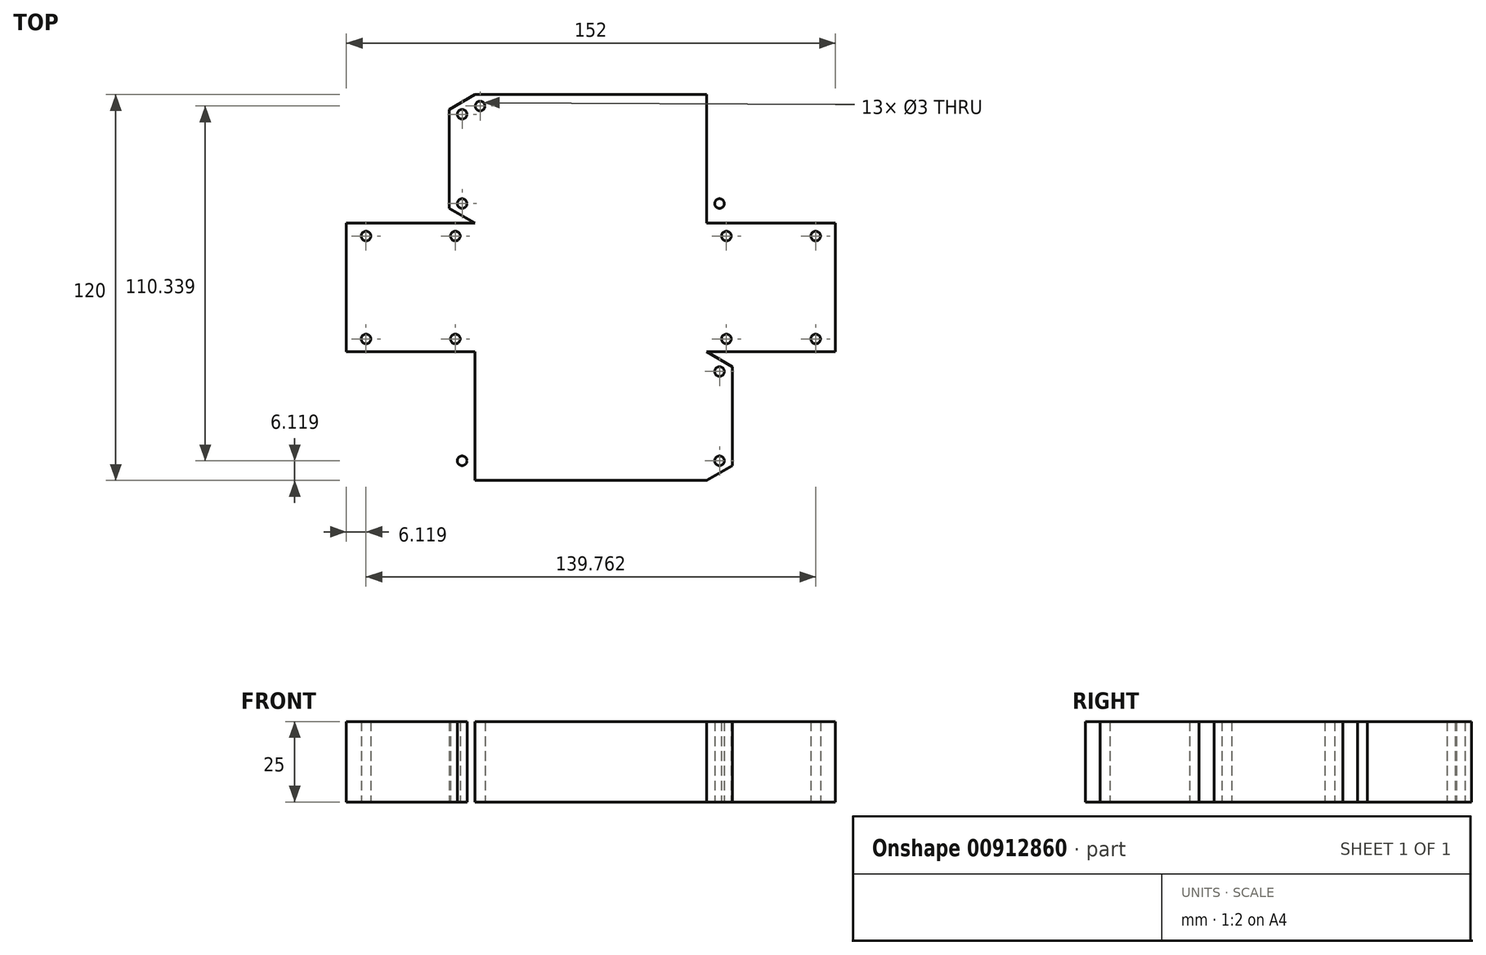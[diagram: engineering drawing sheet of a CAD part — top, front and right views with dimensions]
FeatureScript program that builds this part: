
annotation { "Feature Type Name" : "Feature", "Feature Type Description" : "" }
export const myFeature = defineFeature(function(context is Context, id is Id, definition is map)
    precondition{}
    {
        {
            var Q0;
            Q0=qCreatedBy(makeId("Top.planeOp"),FACE);
            var sketch = newSketch(context, id + "F0", { "sketchPlane" : qUnion([Q0])});
            skLineSegment(sketch, "E0.bottom", {"start": v(-36, 20) * mm, "end": v(36, 20) * mm});
            skLineSegment(sketch, "E0.top", {"start": v(-36, -20) * mm, "end": v(36, -20) * mm});
            skLineSegment(sketch, "E0.left", {"start": v(-36, 20) * mm, "end": v(-36, -20) * mm});
            skLineSegment(sketch, "E0.right", {"start": v(36, 20) * mm, "end": v(36, -20) * mm});
            skPoint(sketch, "E1", {"position": v(0, 20) * mm});
            skPoint(sketch, "E2", {"position": v(-36, 0) * mm});
            skLineSegment(sketch, "E3.bottom", {"start": v(0, 20) * mm, "end": v(-36, 20) * mm});
            skLineSegment(sketch, "E3.top", {"start": v(0, 60) * mm, "end": v(-36, 60) * mm});
            skLineSegment(sketch, "E3.right", {"start": v(-36, 20) * mm, "end": v(-36, 60) * mm});
            skLineSegment(sketch, "E4.bottom", {"start": v(-36, 20) * mm, "end": v(-76, 20) * mm});
            skLineSegment(sketch, "E4.top", {"start": v(-36, -20) * mm, "end": v(-76, -20) * mm});
            skLineSegment(sketch, "E4.right", {"start": v(-76, 20) * mm, "end": v(-76, -20) * mm});
            skLineSegment(sketch, "E5", {"start": v(-36, 60) * mm, "end": v(-44, 55.38) * mm});
            skLineSegment(sketch, "E6", {"start": v(-44, 55.38) * mm, "end": v(-44, 24.62) * mm});
            skLineSegment(sketch, "E7", {"start": v(-44, 24.62) * mm, "end": v(-36, 20) * mm});
            skCircle(sketch, "E8", {"center": v(-69.88, 16) * mm, "radius": 1.5 * mm});
            skCircle(sketch, "E9", {"center": v(-40, 53.88) * mm, "radius": 1.5 * mm});
            skCircle(sketch, "E10", {"center": v(-40, 26.12) * mm, "radius": 1.5 * mm});
            skCircle(sketch, "E11.MirrorC", {"center": v(40, 26.12) * mm, "radius": 1.5 * mm});
            skCircle(sketch, "E12.MirrorC", {"center": v(40, 53.88) * mm, "radius": 1.5 * mm});
            skLineSegment(sketch, "E13.MirrorCS", {"start": v(0, 60) * mm, "end": v(36, 60) * mm});
            skLineSegment(sketch, "E14.MirrorCS", {"start": v(0, 20) * mm, "end": v(36, 20) * mm});
            skLineSegment(sketch, "E15.MirrorCS", {"start": v(44, 24.62) * mm, "end": v(36, 20) * mm});
            skLineSegment(sketch, "E16.MirrorCS", {"start": v(36, 20) * mm, "end": v(36, 60) * mm});
            skLineSegment(sketch, "E17.MirrorCS", {"start": v(44, 55.38) * mm, "end": v(44, 24.62) * mm});
            skLineSegment(sketch, "E18.MirrorCS", {"start": v(36, 60) * mm, "end": v(44, 55.38) * mm});
            skLineSegment(sketch, "E19.MirrorCS", {"start": v(36, 20) * mm, "end": v(-36, 20) * mm});
            skPoint(sketch, "E20.MirrorP", {"position": v(0, -20) * mm});
            skCircle(sketch, "E21.MirrorC", {"center": v(-40, -26.12) * mm, "radius": 1.5 * mm});
            skCircle(sketch, "E22.MirrorC", {"center": v(40, -53.88) * mm, "radius": 1.5 * mm});
            skCircle(sketch, "E23.MirrorC", {"center": v(-40, -53.88) * mm, "radius": 1.5 * mm});
            skCircle(sketch, "E24.MirrorC", {"center": v(40, -26.12) * mm, "radius": 1.5 * mm});
            skLineSegment(sketch, "E25.MirrorCS", {"start": v(0, -20) * mm, "end": v(36, -20) * mm});
            skLineSegment(sketch, "E26.MirrorCS", {"start": v(0, -20) * mm, "end": v(-36, -20) * mm});
            skLineSegment(sketch, "E27.MirrorCS", {"start": v(-44, -55.38) * mm, "end": v(-44, -24.62) * mm});
            skLineSegment(sketch, "E28.MirrorCS", {"start": v(-36, -20) * mm, "end": v(-36, -60) * mm});
            skLineSegment(sketch, "E29.MirrorCS", {"start": v(-36, -60) * mm, "end": v(-44, -55.38) * mm});
            skLineSegment(sketch, "E30.MirrorCS", {"start": v(0, -60) * mm, "end": v(36, -60) * mm});
            skLineSegment(sketch, "E31.MirrorCS", {"start": v(36, -60) * mm, "end": v(44, -55.38) * mm});
            skLineSegment(sketch, "E32.MirrorCS", {"start": v(44, -24.62) * mm, "end": v(36, -20) * mm});
            skLineSegment(sketch, "E33.MirrorCS", {"start": v(0, -60) * mm, "end": v(-36, -60) * mm});
            skLineSegment(sketch, "E34.MirrorCS", {"start": v(-44, -24.62) * mm, "end": v(-36, -20) * mm});
            skLineSegment(sketch, "E35.MirrorCS", {"start": v(36, -20) * mm, "end": v(36, -60) * mm});
            skLineSegment(sketch, "E36.MirrorCS", {"start": v(44, -55.38) * mm, "end": v(44, -24.62) * mm});
            skLineSegment(sketch, "E37.MirrorCS", {"start": v(36, -20) * mm, "end": v(-36, -20) * mm});
            skCircle(sketch, "E38", {"center": v(-42.12, 16) * mm, "radius": 1.5 * mm});
            skCircle(sketch, "E39.MirrorC", {"center": v(-42.12, -16) * mm, "radius": 1.5 * mm});
            skCircle(sketch, "E40.MirrorC", {"center": v(-69.88, -16) * mm, "radius": 1.5 * mm});
            skCircle(sketch, "E41.MirrorC", {"center": v(-34.41, 56.46) * mm, "radius": 1.5 * mm});
            skLineSegment(sketch, "E42.MirrorCS", {"start": v(36, 20) * mm, "end": v(76, 20) * mm});
            skLineSegment(sketch, "E43.MirrorCS", {"start": v(76, 20) * mm, "end": v(76, -20) * mm});
            skLineSegment(sketch, "E44.MirrorCS", {"start": v(36, -20) * mm, "end": v(76, -20) * mm});
            skCircle(sketch, "E45.MirrorC", {"center": v(69.88, 16) * mm, "radius": 1.5 * mm});
            skCircle(sketch, "E46.MirrorC", {"center": v(42.12, -16) * mm, "radius": 1.5 * mm});
            skCircle(sketch, "E47.MirrorC", {"center": v(69.88, -16) * mm, "radius": 1.5 * mm});
            skCircle(sketch, "E48.MirrorC", {"center": v(42.12, 16) * mm, "radius": 1.5 * mm});
            skSolve(sketch);
        }
        {
            var Q0;
            Q0=makeQuery(id+"F0.imprint","IMPRINT",FACE,{"disambiguationData":[TD([[makeQuery(id+"F0.imprint","IMPRINT",EDGE,{"derivedFrom":sQuery(id+"F0.wireOp",EDGE,"E4.bottom")}),1.0]])]});
            var Q1;
            Q1=makeQuery(id+"F0.imprint","IMPRINT",FACE,{"disambiguationData":[TD([[makeQuery(id+"F0.imprint","IMPRINT",EDGE,{"derivedFrom":sQuery(id+"F0.wireOp",EDGE,"E0.right")}),-1.0]])]});
            var Q2;
            Q2=makeQuery(id+"F0.imprint","IMPRINT",FACE,{"disambiguationData":[TD([[makeQuery(id+"F0.imprint","IMPRINT",EDGE,{"derivedFrom":sQuery(id+"F0.wireOp",EDGE,"E35.MirrorCS")}),-1.0]])]});
            var Q3;
            Q3=makeQuery(id+"F0.imprint","IMPRINT",FACE,{"disambiguationData":[TD([[makeQuery(id+"F0.imprint","IMPRINT",EDGE,{"derivedFrom":sQuery(id+"F0.wireOp",EDGE,"E23.MirrorC")}),1.0]])]});
            var Q4;
            Q4=makeQuery(id+"F0.imprint","IMPRINT",FACE,{"disambiguationData":[TD([[makeQuery(id+"F0.imprint","IMPRINT",EDGE,{"derivedFrom":sQuery(id+"F0.wireOp",EDGE,"E22.MirrorC")}),-1.0]])]});
            var Q5;
            Q5=makeQuery(id+"F0.imprint","IMPRINT",FACE,{"disambiguationData":[TD([[makeQuery(id+"F0.imprint","IMPRINT",EDGE,{"derivedFrom":sQuery(id+"F0.wireOp",EDGE,"E3.top")}),1.0]])]});
            var Q6;
            Q6=makeQuery(id+"F0.imprint","IMPRINT",FACE,{"disambiguationData":[TD([[makeQuery(id+"F0.imprint","IMPRINT",EDGE,{"derivedFrom":sQuery(id+"F0.wireOp",EDGE,"E7")}),1.0]])]});
            var Q7;
            Q7=makeQuery(id+"F0.imprint","IMPRINT",FACE,{"disambiguationData":[TD([[makeQuery(id+"F0.imprint","IMPRINT",EDGE,{"derivedFrom":sQuery(id+"F0.wireOp",EDGE,"E0.right")}),1.0]])]});
            var Q8;
            Q8=makeQuery(id+"F0.imprint","IMPRINT",FACE,{"disambiguationData":[TD([[makeQuery(id+"F0.imprint","IMPRINT",EDGE,{"derivedFrom":sQuery(id+"F0.wireOp",EDGE,"E11.MirrorC")}),1.0]])]});
            extrude(context, id + "F1", {"entities" : qUnion([Q0, Q1, Q2, Q3, Q4, Q5, Q6, Q7, Q8]), "depth" : 25 * mm, "offsetDistance" : 25 * mm});
        }
    });
